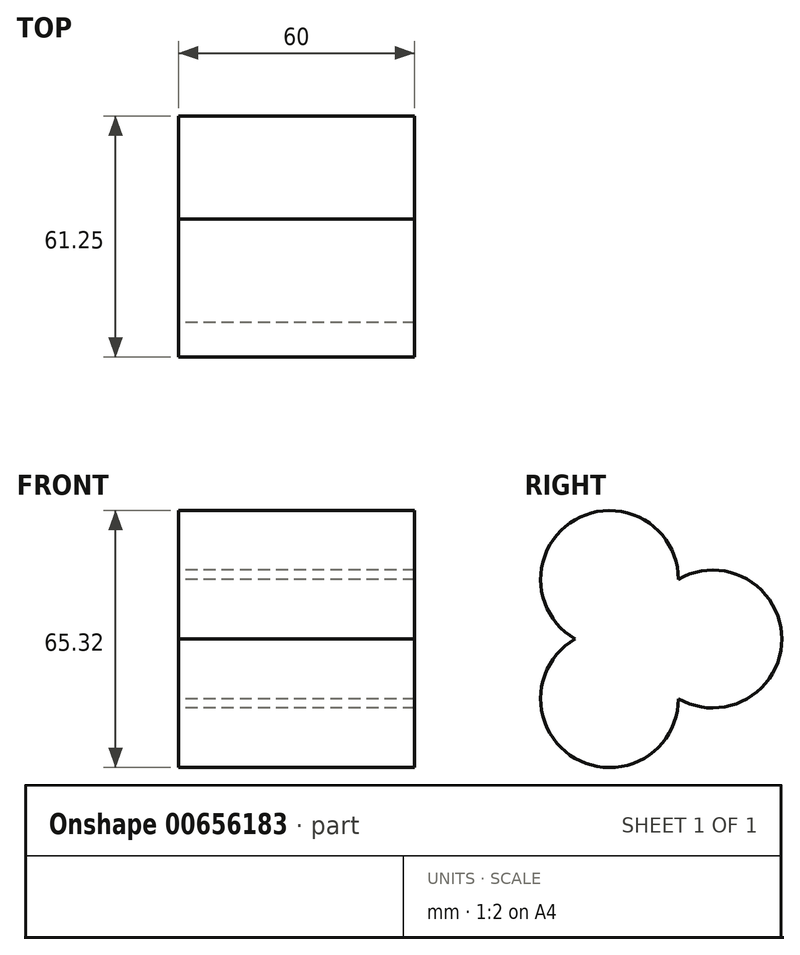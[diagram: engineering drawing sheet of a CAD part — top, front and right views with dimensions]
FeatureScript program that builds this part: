
annotation { "Feature Type Name" : "Feature", "Feature Type Description" : "" }
export const myFeature = defineFeature(function(context is Context, id is Id, definition is map)
    precondition{}
    {
        {
            var Q0;
            Q0=qCreatedBy(makeId("Right.planeOp"),FACE);
            var sketch = newSketch(context, id + "F0", { "sketchPlane" : qUnion([Q0])});
            skCircle(sketch, "E0", {"center": v(0, 0) * mm, "radius": 35 * mm});
            skLineSegment(sketch, "E1", {"start": v(0, 0) * mm, "end": v(35, 0) * mm});
            skLineSegment(sketch, "E2", {"start": v(0, 0) * mm, "end": v(-17.5, 30.31) * mm});
            skLineSegment(sketch, "E3", {"start": v(0, 0) * mm, "end": v(-17.5, -30.31) * mm});
            skCircle(sketch, "E4", {"center": v(17.5, 0) * mm, "radius": 17.5 * mm});
            skCircle(sketch, "E5", {"center": v(-8.75, 15.16) * mm, "radius": 17.5 * mm});
            skCircle(sketch, "E6", {"center": v(-8.75, -15.16) * mm, "radius": 17.5 * mm});
            skSolve(sketch);
        }
        {
            var Q0;
            {var subQ0=sQuery(id+"F0.wireOp",EDGE,"E2");Q0=makeQuery(id+"F0.imprint","IMPRINT",FACE,{"disambiguationData":[TD([[makeQuery(id+"F0.imprint","IMPRINT",EDGE,{"derivedFrom":subQ0}),1.0]])]});}
            var Q1;
            {var subQ0=sQuery(id+"F0.wireOp",EDGE,"E3");Q1=makeQuery(id+"F0.imprint","IMPRINT",FACE,{"disambiguationData":[TD([[makeQuery(id+"F0.imprint","IMPRINT",EDGE,{"derivedFrom":subQ0}),1.0]])]});}
            var Q2;
            {var subQ0=sQuery(id+"F0.wireOp",EDGE,"E3");Q2=makeQuery(id+"F0.imprint","IMPRINT",FACE,{"disambiguationData":[TD([[makeQuery(id+"F0.imprint","IMPRINT",EDGE,{"derivedFrom":subQ0}),-1.0]])]});}
            var Q3;
            {var subQ0=sQuery(id+"F0.wireOp",EDGE,"E1");Q3=makeQuery(id+"F0.imprint","IMPRINT",FACE,{"disambiguationData":[TD([[makeQuery(id+"F0.imprint","IMPRINT",EDGE,{"derivedFrom":subQ0}),1.0]])]});}
            var Q4;
            {var subQ0=sQuery(id+"F0.wireOp",EDGE,"E1");Q4=makeQuery(id+"F0.imprint","IMPRINT",FACE,{"disambiguationData":[TD([[makeQuery(id+"F0.imprint","IMPRINT",EDGE,{"derivedFrom":subQ0}),-1.0]])]});}
            var Q5;
            {var subQ0=sQuery(id+"F0.wireOp",EDGE,"E2");Q5=makeQuery(id+"F0.imprint","IMPRINT",FACE,{"disambiguationData":[TD([[makeQuery(id+"F0.imprint","IMPRINT",EDGE,{"derivedFrom":subQ0}),-1.0]])]});}
            var Q6;
            {var subQ0=sQuery(id+"F0.wireOp",EDGE,"E6");var subQ1=sQuery(id+"F0.wireOp",EDGE,"E5");var subQ3=makeQuery(id+"F0.imprint","INTERSECT",VERTEX,{"derivedFrom":[subQ1,subQ0]});Q6=makeQuery(id+"F0.imprint","IMPRINT",FACE,{"disambiguationData":[TD([[makeQuery(id+"F0.imprint","IMPRINT",EDGE,{"disambiguationData":[TD([[subQ3,-1.0]])],"derivedFrom":subQ1}),1.0]])]});}
            var Q7;
            {var subQ0=sQuery(id+"F0.wireOp",EDGE,"E5");var subQ1=sQuery(id+"F0.wireOp",EDGE,"E4");var subQ3=makeQuery(id+"F0.imprint","INTERSECT",VERTEX,{"derivedFrom":[subQ1,subQ0]});Q7=makeQuery(id+"F0.imprint","IMPRINT",FACE,{"disambiguationData":[TD([[makeQuery(id+"F0.imprint","IMPRINT",EDGE,{"disambiguationData":[TD([[subQ3,-1.0]])],"derivedFrom":subQ1}),1.0]])]});}
            var Q8;
            {var subQ0=sQuery(id+"F0.wireOp",EDGE,"E6");var subQ1=sQuery(id+"F0.wireOp",EDGE,"E4");var subQ3=makeQuery(id+"F0.imprint","INTERSECT",VERTEX,{"derivedFrom":[subQ1,subQ0]});Q8=makeQuery(id+"F0.imprint","IMPRINT",FACE,{"disambiguationData":[TD([[makeQuery(id+"F0.imprint","IMPRINT",EDGE,{"disambiguationData":[TD([[subQ3,1.0]])],"derivedFrom":subQ1}),1.0]])]});}
            extrude(context, id + "F1", {"entities" : qUnion([Q0, Q1, Q2, Q3, Q4, Q5, Q6, Q7, Q8]), "depth" : 60 * mm, "offsetDistance" : 25 * mm});
        }
    });
